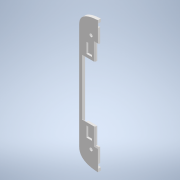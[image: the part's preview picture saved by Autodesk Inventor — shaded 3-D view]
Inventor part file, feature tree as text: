
AUTODESK INVENTOR PART (.ipt)
format: ipt  version: 2022 (Build 260153000, 153)  size: 340,992 bytes
history: native  units: mm
features: other x6, extrude x6, sketch x6, reference x6, projected_geometry x4, chamfer x1, mirror x1
ambient origin geometry x8: Origin, YZ Plane, XZ Plane, XY Plane, X Axis, Y Axis, Z Axis, Center Point
bodies: Body1 (feature_tree)
feature tree (30):
  other  "Твердое тело1"
  extrude  "Выдавливание1"  Depth=3.0mm
  extrude  "Выдавливание3"  Depth=3.0mm TaperAngle=0.0deg
  extrude  "Выдавливание4"  Depth=0.3mm
  extrude  "Выдавливание5"  Depth=0.4mm TaperAngle=0.0deg
  extrude  "Выдавливание7"  Depth=3.2mm
  extrude  "Выдавливание8"  Depth=3.2mm
  chamfer  "Фаска3"  Distance=1.0mm
  mirror  "Зеркальное отражение1"
  sketch  "Эскиз1"
  reference  "Ссылка1"
  reference  "Ссылка2"
  sketch  "Эскиз3"
  projected_geometry  "Спроецированная петля2"
  reference  "Ссылка4"
  reference  "Ссылка5"
  sketch  "Эскиз4"
  reference  "Ссылка6"
  sketch  "Эскиз5"
  projected_geometry  "Спроецированная петля3"
  sketch  "Эскиз7"
  projected_geometry  "Спроецированная петля6"
  sketch  "Эскиз8"
  projected_geometry  "Спроецированная петля7"
  reference  "Ссылка7"
  other  "<userpath>\Documents\Git\MZCAT_2024\MZCAT_4.iam"
  other  "MZCAT_4.iam"
  other  "CAT_protector:1"
  other  "magazine_fixator:1"
  other  "left_back_cup:1"
